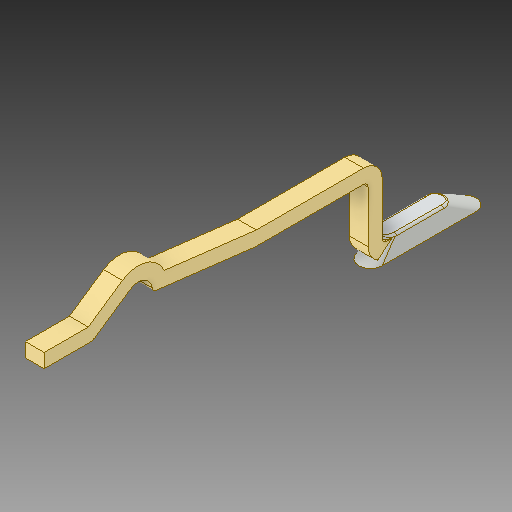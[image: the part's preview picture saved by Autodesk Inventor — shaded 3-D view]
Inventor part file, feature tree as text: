
AUTODESK INVENTOR PART (.ipt)
format: ipt  version: 2019.4 (Build 234330000, 330)  size: 162,816 bytes
history: native  units: mm
features: fillet x1
ambient origin geometry x8: Origin, YZ Plane, XZ Plane, XY Plane, X Axis, Y Axis, Z Axis, Center Point
bodies: Solid1 (feature_tree)
feature tree (1):
  fillet  "Fillet2"  [1 undecoded]
note: 1 required parameter value undecoded (feature->parameter linkage not recoverable at this tier; creation-order binding heuristic only, values carry confidence <= 0.55)
